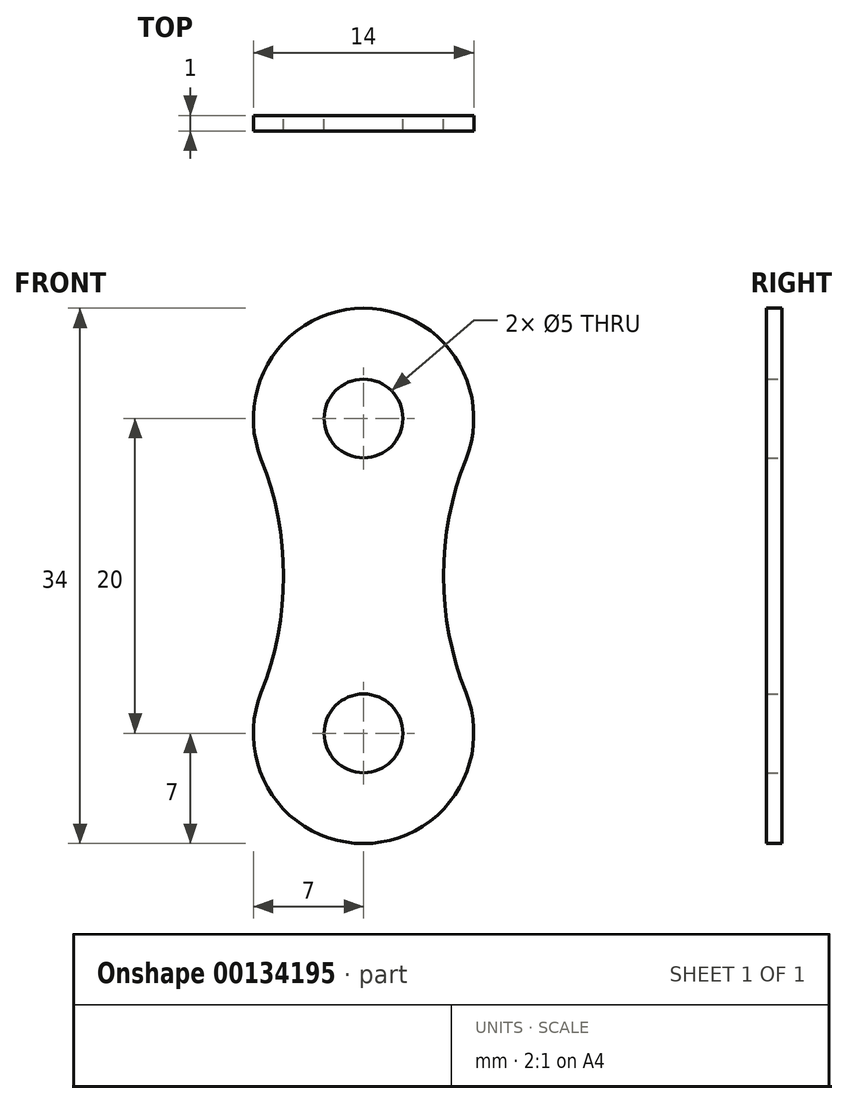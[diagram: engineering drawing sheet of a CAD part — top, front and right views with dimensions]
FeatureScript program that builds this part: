
annotation { "Feature Type Name" : "Feature", "Feature Type Description" : "" }
export const myFeature = defineFeature(function(context is Context, id is Id, definition is map)
    precondition{}
    {
        {
            var Q0;
            Q0=qCreatedBy(makeId("Front.planeOp"),FACE);
            var sketch = newSketch(context, id + "F0", { "sketchPlane" : qUnion([Q0])});
            skArc(sketch, "E0", {"start": v(6.5, -2.6) * mm, "mid": v(0, 7) * mm, "end": v(-6.5, -2.6) * mm});
            skCircle(sketch, "E1", {"center": v(0, 0) * mm, "radius": 2.5 * mm});
            skCircle(sketch, "E2", {"center": v(0, -20) * mm, "radius": 2.5 * mm});
            skArc(sketch, "E3", {"start": v(-6.5, -17.4) * mm, "mid": v(0, -27) * mm, "end": v(6.5, -17.4) * mm});
            skArc(sketch, "E4", {"start": v(-6.5, -17.4) * mm, "mid": v(-5.08, -10) * mm, "end": v(-6.5, -2.6) * mm});
            skArc(sketch, "E5", {"start": v(6.5, -2.6) * mm, "mid": v(5.08, -10) * mm, "end": v(6.5, -17.4) * mm});
            skSolve(sketch);
        }
        {
            var Q0;
            Q0=makeQuery(id+"F0.imprint","IMPRINT",FACE,{"disambiguationData":[TD([[makeQuery(id+"F0.imprint","IMPRINT",EDGE,{"derivedFrom":sQuery(id+"F0.wireOp",EDGE,"E0")}),1.0]])]});
            extrude(context, id + "F1", {"entities" : qUnion([Q0]), "depth" : 1 * mm});
        }
    });
